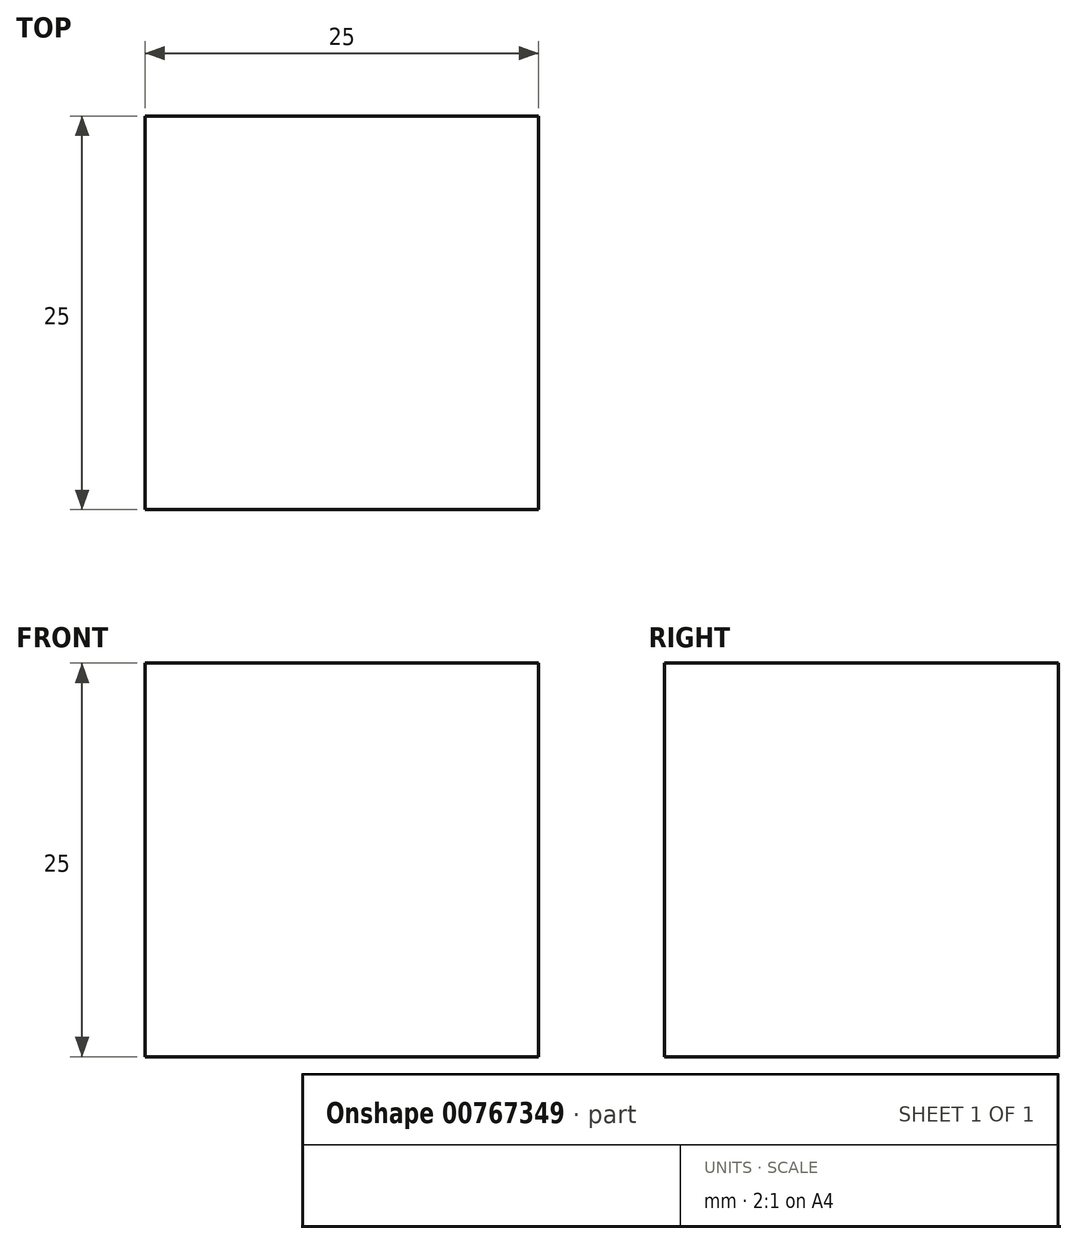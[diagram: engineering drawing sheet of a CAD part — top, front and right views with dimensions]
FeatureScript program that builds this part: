
annotation { "Feature Type Name" : "Feature", "Feature Type Description" : "" }
export const myFeature = defineFeature(function(context is Context, id is Id, definition is map)
    precondition{}
    {
        {
            var Q0;
            Q0=qCreatedBy(makeId("Top.planeOp"),FACE);
            var sketch = newSketch(context, id + "F0", { "sketchPlane" : qUnion([Q0])});
            skLineSegment(sketch, "E0.bottom", {"start": v(12.5, -12.5) * mm, "end": v(-12.5, -12.5) * mm});
            skLineSegment(sketch, "E0.top", {"start": v(12.5, 12.5) * mm, "end": v(-12.5, 12.5) * mm});
            skLineSegment(sketch, "E0.left", {"start": v(12.5, -12.5) * mm, "end": v(12.5, 12.5) * mm});
            skLineSegment(sketch, "E0.right", {"start": v(-12.5, -12.5) * mm, "end": v(-12.5, 12.5) * mm});
            skPoint(sketch, "E0.middle", {"position": v(0, 0) * mm});
            skSolve(sketch);
        }
        {
            var Q0;
            Q0=makeQuery(id+"F0.imprint","IMPRINT",FACE,{"disambiguationData":[TD([[makeQuery(id+"F0.imprint","IMPRINT",EDGE,{"derivedFrom":sQuery(id+"F0.wireOp",EDGE,"E0.bottom")}),-1.0]])]});
            extrude(context, id + "F1", {"entities" : qUnion([Q0]), "depth" : 25 * mm, "offsetDistance" : 25 * mm});
        }
    });
